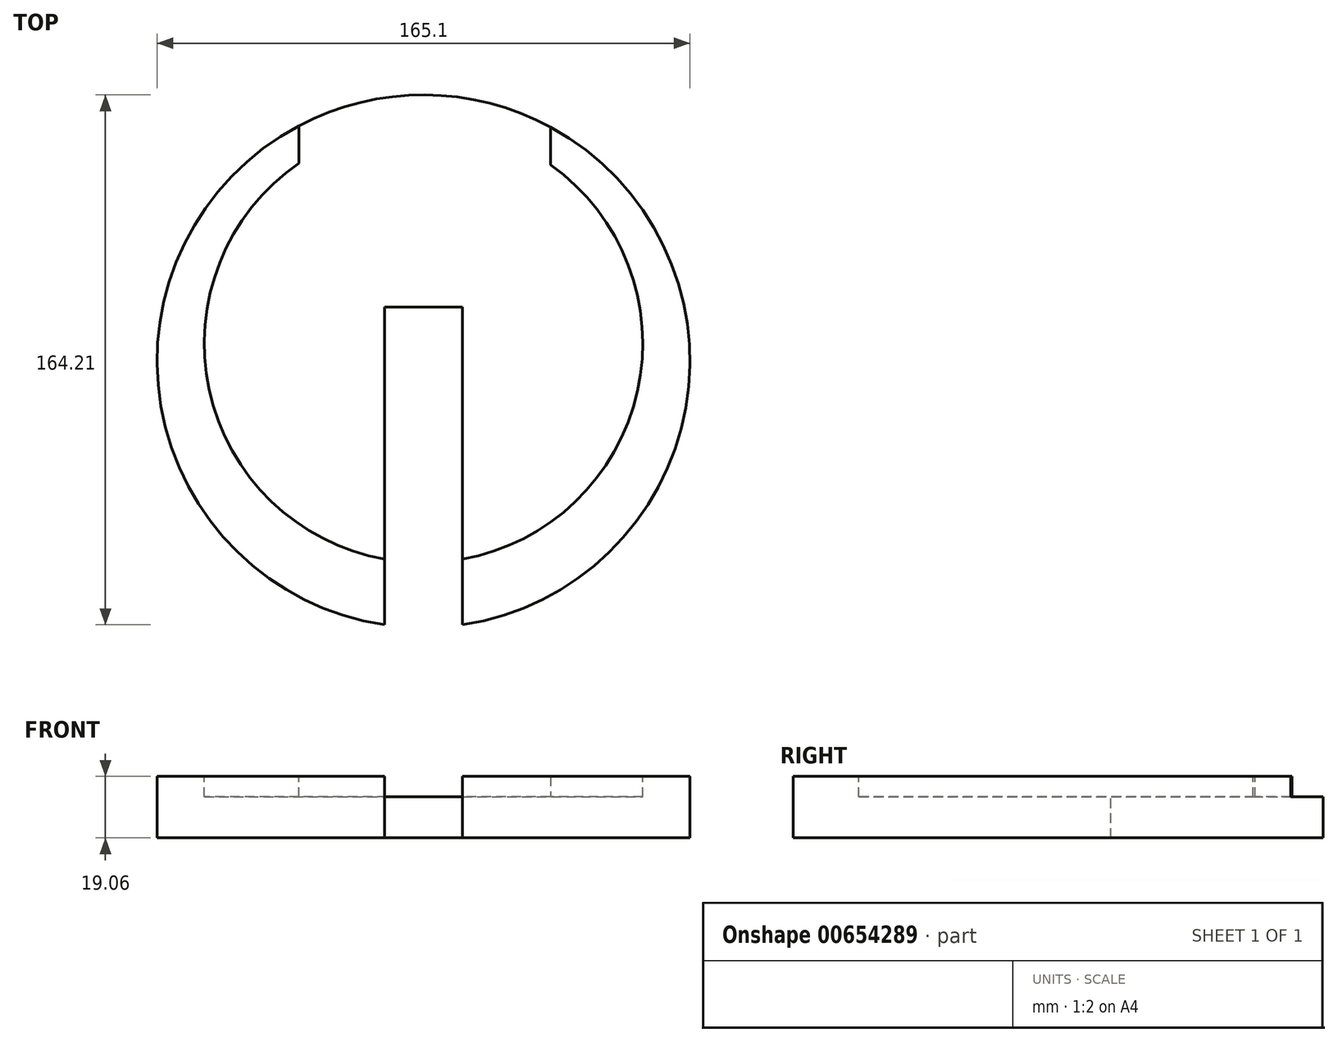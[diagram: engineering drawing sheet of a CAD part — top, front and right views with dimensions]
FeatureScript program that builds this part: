
annotation { "Feature Type Name" : "Feature", "Feature Type Description" : "" }
export const myFeature = defineFeature(function(context is Context, id is Id, definition is map)
    precondition{}
    {
        {
            var Q0;
            Q0=qCreatedBy(makeId("Top.planeOp"),FACE);
            var sketch = newSketch(context, id + "F0", { "sketchPlane" : qUnion([Q0])});
            skCircle(sketch, "E0", {"center": v(0, 0) * mm, "radius": 82.55 * mm});
            skSolve(sketch);
        }
        {
            var Q0;
            Q0=qSketchRegion(id+"F0",true);
            extrude(context, id + "F1", {"entities" : qUnion([Q0]), "endBound" : BoundingType.SYMMETRIC, "depth" : 19.05 * mm, "offsetDistance" : 25.4 * mm});
        }
        {
            var Q0;
            Q0=qCreatedBy(makeId("Top.planeOp"),FACE);
            var sketch = newSketch(context, id + "F2", { "sketchPlane" : qUnion([Q0])});
            skLineSegment(sketch, "E1.top", {"start": v(12.07, -82.62) * mm, "end": v(-12.06, -82.62) * mm});
            skPoint(sketch, "E1.middle", {"position": v(0, 0) * mm});
            skLineSegment(sketch, "E2", {"start": v(-12.06, 16.82) * mm, "end": v(12.07, 16.82) * mm});
            skLineSegment(sketch, "E3", {"start": v(-12.06, 16.82) * mm, "end": v(-12.06, -82.62) * mm});
            skLineSegment(sketch, "E4", {"start": v(12.07, 16.82) * mm, "end": v(12.07, -82.62) * mm});
            skSolve(sketch);
        }
        {
            var Q0;
            Q0=qSketchRegion(id+"F2",true);
            extrude(context, id + "F3", {"entities" : qUnion([Q0]), "operationType" : NewBodyOperationType.REMOVE, "endBound" : BoundingType.SYMMETRIC, "oppositeDirection" : true, "depth" : 19.05 * mm, "offsetDistance" : 25.4 * mm});
        }
        {
            var Q0;
            Q0=makeQuery(id+"F1.opExtrude","CAP_FACE",FACE,{"disambiguationData":[OSD([sQuery(id+"F0.wireOp",EDGE,"E0")])],"isStart":false});
            cPlane(context, id + "F4", {"entities" : qUnion([Q0]), "cplaneType" : CPlaneType.OFFSET, "offset" : 0 * mm, "width" : 152.4 * mm, "height" : 152.4 * mm});
        }
        {
            var Q0;
            Q0=makeQuery(id+"F1.opExtrude","CAP_FACE",FACE,{"disambiguationData":[OSD([sQuery(id+"F0.wireOp",EDGE,"E0")])],"isStart":false});
            var sketch = newSketch(context, id + "F5", { "sketchPlane" : qUnion([Q0])});
            skCircle(sketch, "E5", {"center": v(0, 5.51) * mm, "radius": 67.95 * mm});
            skSolve(sketch);
        }
        {
            var Q0;
            Q0 = qSketchRegion(id + "F5", true);
            extrude(context, id + "F6", {"entities" : qUnion([Q0]), "operationType" : NewBodyOperationType.REMOVE, "oppositeDirection" : true, "depth" : 6.35 * mm, "offsetDistance" : 25.4 * mm});
        }
        {
            var Q0;
            Q0=qCreatedBy(id+"F4.planeOp",FACE);
            var sketch = newSketch(context, id + "F7", { "sketchPlane" : qUnion([Q0])});
            skLineSegment(sketch, "E6", {"start": v(6.1, 103.54) * mm, "end": v(-38.6, 103.54) * mm});
            skLineSegment(sketch, "E7", {"start": v(-38.6, 103.54) * mm, "end": v(-38.6, 52.74) * mm});
            skLineSegment(sketch, "E8", {"start": v(-38.6, 52.74) * mm, "end": v(39.37, 52.74) * mm});
            skLineSegment(sketch, "E9", {"start": v(39.37, 52.74) * mm, "end": v(39.37, 103.54) * mm});
            skLineSegment(sketch, "E10", {"start": v(39.37, 103.54) * mm, "end": v(6.1, 103.54) * mm});
            skSolve(sketch);
        }
        {
            var Q0;
            Q0 = qSketchRegion(id + "F7", true);
            extrude(context, id + "F8", {"entities" : qUnion([Q0]), "operationType" : NewBodyOperationType.REMOVE, "oppositeDirection" : true, "depth" : 6.35 * mm, "offsetDistance" : 25.4 * mm});
        }
    });
